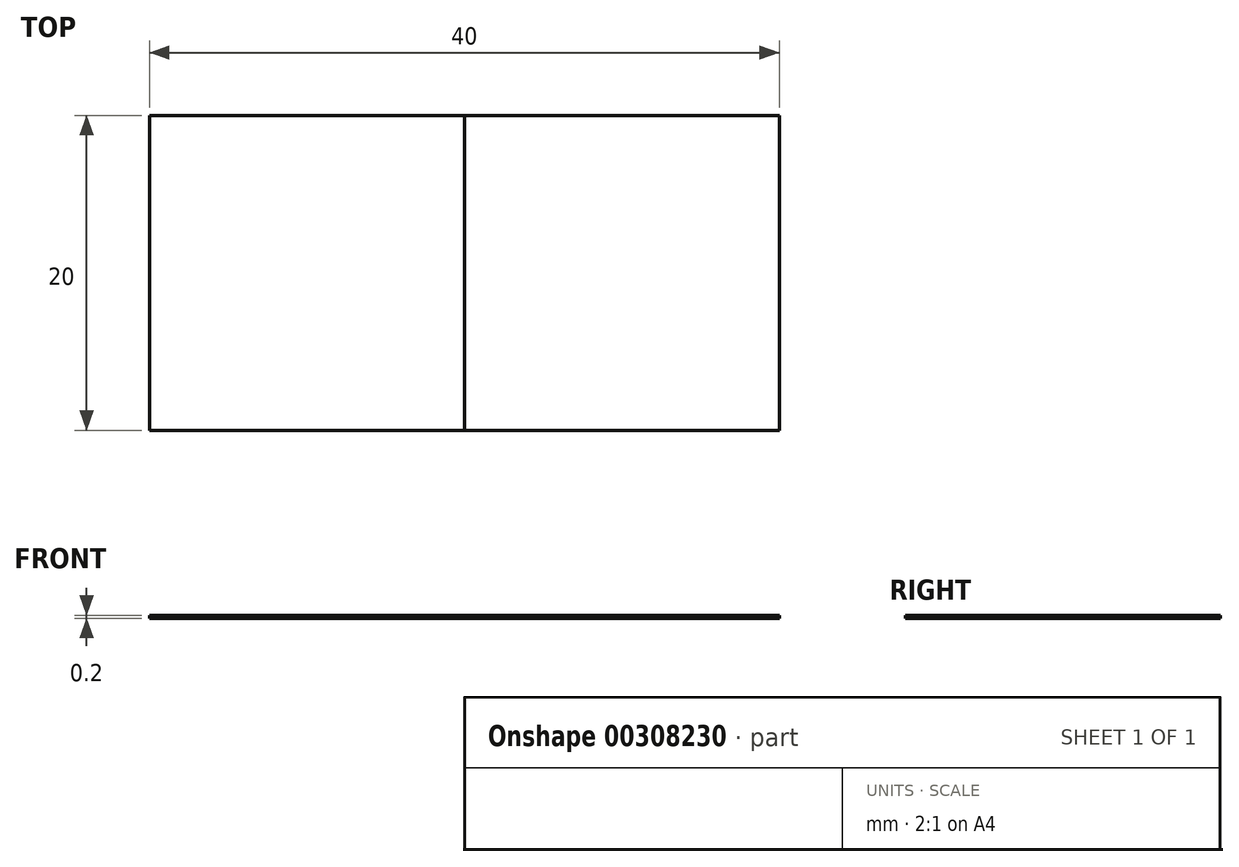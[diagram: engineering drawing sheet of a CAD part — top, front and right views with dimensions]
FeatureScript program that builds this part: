
annotation { "Feature Type Name" : "Feature", "Feature Type Description" : "" }
export const myFeature = defineFeature(function(context is Context, id is Id, definition is map)
    precondition{}
    {
        {
            var Q0;
            Q0=qCreatedBy(makeId("Top.planeOp"),FACE);
            var sketch = newSketch(context, id + "F0", { "sketchPlane" : qUnion([Q0])});
            skLineSegment(sketch, "E0.bottom", {"start": v(20, 10) * mm, "end": v(-20, 10) * mm});
            skLineSegment(sketch, "E0.top", {"start": v(20, -10) * mm, "end": v(-20, -10) * mm});
            skLineSegment(sketch, "E0.left", {"start": v(20, 10) * mm, "end": v(20, -10) * mm});
            skLineSegment(sketch, "E0.right", {"start": v(-20, 10) * mm, "end": v(-20, -10) * mm});
            skPoint(sketch, "E0.middle", {"position": v(0, 0) * mm});
            skLineSegment(sketch, "E1", {"start": v(0, -10) * mm, "end": v(0, 10) * mm});
            skSolve(sketch);
        }
        {
            var Q0;
            {var subQ0=sQuery(id+"F0.wireOp",EDGE,"E0.right");Q0=makeQuery(id+"F0.imprint","IMPRINT",FACE,{"disambiguationData":[TD([[makeQuery(id+"F0.imprint","IMPRINT",EDGE,{"derivedFrom":subQ0}),1.0]])]});}
            extrude(context, id + "F1", {"entities" : qUnion([Q0]), "depth" : .2 * mm, "offsetDistance" : 25 * mm});
        }
        {
            var Q0;
            {var subQ0=sQuery(id+"F0.wireOp",EDGE,"E0.left");Q0=makeQuery(id+"F0.imprint","IMPRINT",FACE,{"disambiguationData":[TD([[makeQuery(id+"F0.imprint","IMPRINT",EDGE,{"derivedFrom":subQ0}),-1.0]])]});}
            extrude(context, id + "F2", {"entities" : qUnion([Q0]), "depth" : .2 * mm, "offsetDistance" : 25 * mm});
        }
    });
